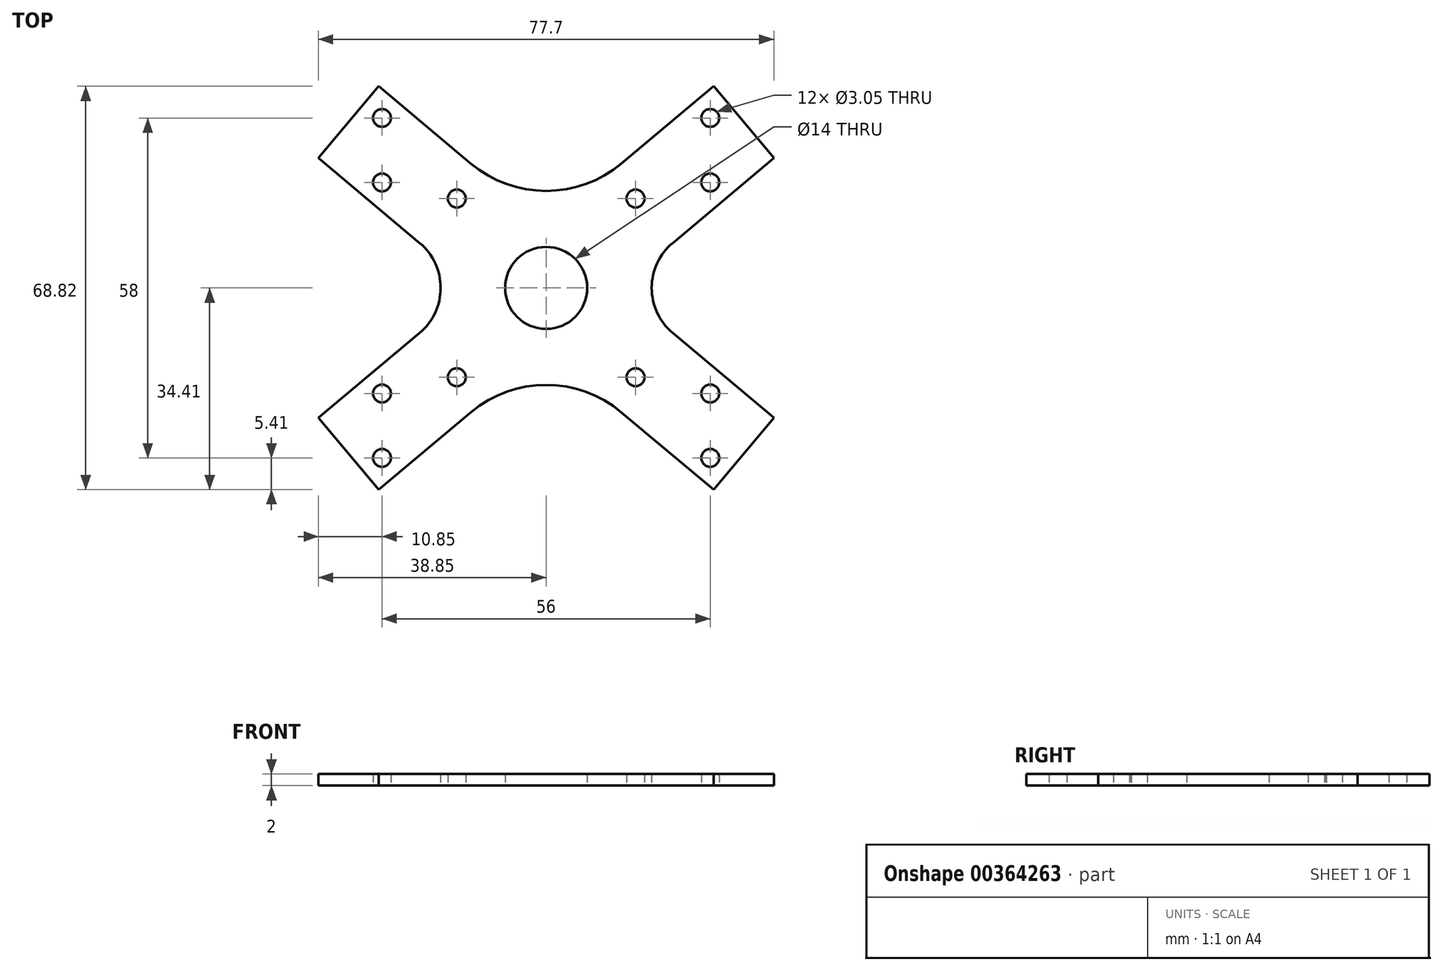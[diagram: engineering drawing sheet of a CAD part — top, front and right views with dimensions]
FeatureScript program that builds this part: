
annotation { "Feature Type Name" : "Feature", "Feature Type Description" : "" }
export const myFeature = defineFeature(function(context is Context, id is Id, definition is map)
    precondition{}
    {
        {
            var Q0;
            Q0=qCreatedBy(makeId("Top.planeOp"),FACE);
            var sketch = newSketch(context, id + "F0", { "sketchPlane" : qUnion([Q0])});
            skLineSegment(sketch, "E0", {"start": v(-28.56, 34.41) * mm, "end": v(-38.85, 22.15) * mm});
            skLineSegment(sketch, "E1", {"start": v(-38.85, 22.15) * mm, "end": v(-21.58, 7.66) * mm});
            skLineSegment(sketch, "E2", {"start": v(-28.56, 34.41) * mm, "end": v(-12.86, 21.23) * mm});
            skLineSegment(sketch, "E3", {"start": v(-82.35, 69.1) * mm, "end": v(0, 0) * mm, "construction": true});
            skCircle(sketch, "E4", {"center": v(0, 0) * mm, "radius": 107.5 * mm, "construction": true});
            skCircle(sketch, "E5", {"center": v(-28, 29) * mm, "radius": 1.52 * mm});
            skCircle(sketch, "E6", {"center": v(-28, 18) * mm, "radius": 1.52 * mm});
            skCircle(sketch, "E7", {"center": v(-15.25, 15.25) * mm, "radius": 1.52 * mm});
            skCircle(sketch, "E8.MirrorC", {"center": v(28, 29) * mm, "radius": 1.52 * mm});
            skCircle(sketch, "E9.MirrorC", {"center": v(15.25, 15.25) * mm, "radius": 1.52 * mm});
            skCircle(sketch, "E10.MirrorC", {"center": v(28, 18) * mm, "radius": 1.52 * mm});
            skLineSegment(sketch, "E11.MirrorCS", {"start": v(28.56, 34.41) * mm, "end": v(38.85, 22.15) * mm});
            skLineSegment(sketch, "E12.MirrorCS", {"start": v(38.85, 22.15) * mm, "end": v(21.58, 7.66) * mm});
            skLineSegment(sketch, "E13.MirrorCS", {"start": v(28.56, 34.41) * mm, "end": v(12.86, 21.23) * mm});
            skLineSegment(sketch, "E14.MirrorCS", {"start": v(82.35, 69.1) * mm, "end": v(0, 0) * mm, "construction": true});
            skCircle(sketch, "E15.MirrorC", {"center": v(-28, -18) * mm, "radius": 1.52 * mm});
            skCircle(sketch, "E16.MirrorC", {"center": v(28, -29) * mm, "radius": 1.52 * mm});
            skCircle(sketch, "E17.MirrorC", {"center": v(-15.25, -15.25) * mm, "radius": 1.52 * mm});
            skCircle(sketch, "E18.MirrorC", {"center": v(15.25, -15.25) * mm, "radius": 1.52 * mm});
            skCircle(sketch, "E19.MirrorC", {"center": v(28, -18) * mm, "radius": 1.52 * mm});
            skCircle(sketch, "E20.MirrorC", {"center": v(-28, -29) * mm, "radius": 1.52 * mm});
            skLineSegment(sketch, "E21.MirrorCS", {"start": v(-38.85, -22.15) * mm, "end": v(-21.58, -7.66) * mm});
            skLineSegment(sketch, "E22.MirrorCS", {"start": v(-28.56, -34.41) * mm, "end": v(-12.86, -21.23) * mm});
            skLineSegment(sketch, "E23.MirrorCS", {"start": v(38.85, -22.15) * mm, "end": v(21.58, -7.66) * mm});
            skLineSegment(sketch, "E24.MirrorCS", {"start": v(28.56, -34.41) * mm, "end": v(38.85, -22.15) * mm});
            skLineSegment(sketch, "E25.MirrorCS", {"start": v(-28.56, -34.41) * mm, "end": v(-38.85, -22.15) * mm});
            skLineSegment(sketch, "E26.MirrorCS", {"start": v(28.56, -34.41) * mm, "end": v(12.86, -21.23) * mm});
            skPoint(sketch, "E27.visualSharp", {"position": v(-12.45, 0) * mm});
            skArc(sketch, "E27.filletArc", {"start": v(-21.58, -7.66) * mm, "mid": v(-18, 0) * mm, "end": v(-21.58, 7.66) * mm});
            skPoint(sketch, "E28.visualSharp", {"position": v(12.45, 0) * mm});
            skArc(sketch, "E28.filletArc", {"start": v(21.58, 7.66) * mm, "mid": v(18, 0) * mm, "end": v(21.58, -7.66) * mm});
            skCircle(sketch, "E29", {"center": v(-82.35, 69.1) * mm, "radius": 63.5 * mm, "construction": true});
            skPoint(sketch, "E30.visualSharp", {"position": v(0, 10.44) * mm});
            skArc(sketch, "E30.filletArc", {"start": v(-12.86, 21.23) * mm, "mid": v(0, 16.55) * mm, "end": v(12.86, 21.23) * mm});
            skPoint(sketch, "E31.visualSharp", {"position": v(0, -10.44) * mm});
            skArc(sketch, "E31.filletArc", {"start": v(12.86, -21.23) * mm, "mid": v(0, -16.55) * mm, "end": v(-12.86, -21.23) * mm});
            skCircle(sketch, "E32", {"center": v(0, 0) * mm, "radius": 7 * mm});
            skCircle(sketch, "E33", {"center": v(-28, 29) * mm, "radius": 3 * mm, "construction": true});
            skSolve(sketch);
        }
        {
            var Q0;
            Q0=qSketchRegion(id+"F0",true);
            extrude(context, id + "F1", {"entities" : qUnion([Q0]), "depth" : 2 * mm});
        }
    });
